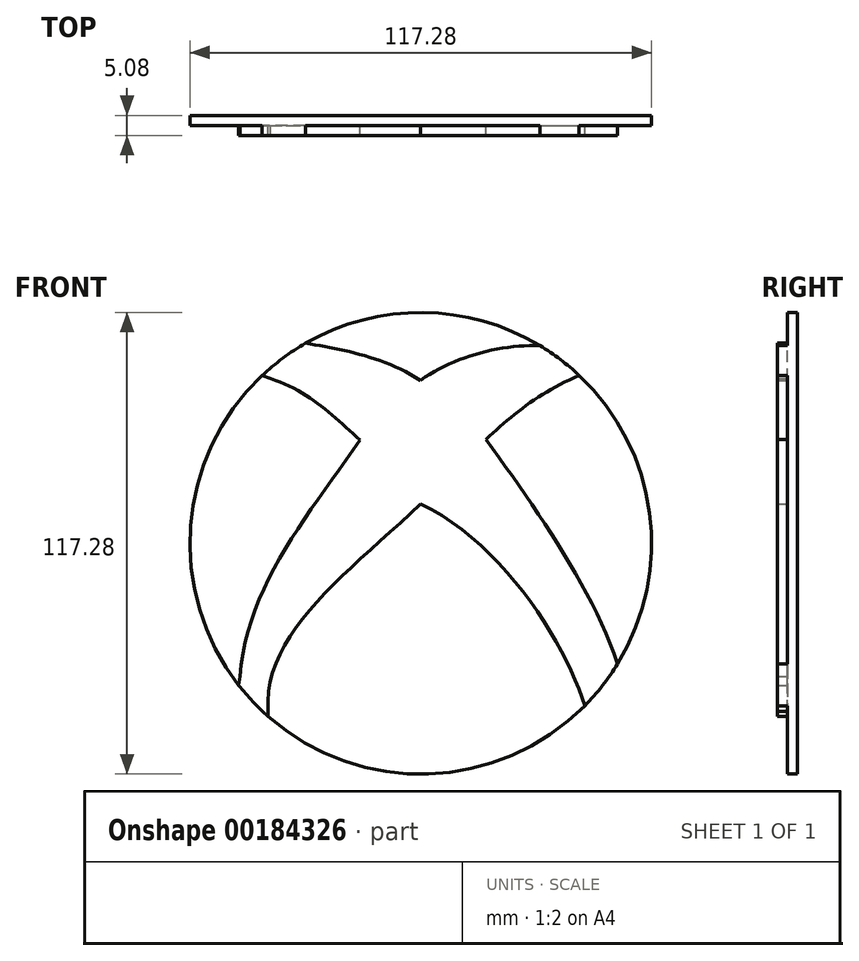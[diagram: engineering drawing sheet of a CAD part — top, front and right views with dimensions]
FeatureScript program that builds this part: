
annotation { "Feature Type Name" : "Feature", "Feature Type Description" : "" }
export const myFeature = defineFeature(function(context is Context, id is Id, definition is map)
    precondition{}
    {
        {
            var Q0;
            Q0=qCreatedBy(makeId("Front.planeOp"),FACE);
            var sketch = newSketch(context, id + "F0", { "sketchPlane" : qUnion([Q0])});
            skCircle(sketch, "E0", {"center": v(0, 0) * mm, "radius": 58.64 * mm});
            skPoint(sketch, "E1.1.internal.orphan", {"position": v(-4.16, 0) * mm});
            skPoint(sketch, "E1.2.internal.orphan", {"position": v(-4.36, 0) * mm});
            skFitSpline(sketch, "E2", {"points": [v(-38.19, 41.82) * mm, v(-15.47, 26.2) * mm], "startDerivative": vector(29.2, -9.13) * mm, "endDerivative": vector(20.69, -18.86) * mm});
            skFitSpline(sketch, "E3", {"points": [v(-15.47, 26.2) * mm, v(-45.9, -33.83) * mm], "startDerivative": vector(-40.16, -58.41) * mm, "endDerivative": vector(-4.87, -68.15) * mm});
            skFitSpline(sketch, "E4", {"points": [v(-38.8, -42.75) * mm, v(0, 9.98) * mm], "startDerivative": vector(-3.65, 59.63) * mm, "endDerivative": vector(59.8, 55.98) * mm});
            skFitSpline(sketch, "E5", {"points": [v(0, 9.98) * mm, v(41.66, -41.27) * mm], "startDerivative": vector(63.1, -29.94) * mm, "endDerivative": vector(14.55, -46.75) * mm});
            skFitSpline(sketch, "E6", {"points": [v(16.57, 26.4) * mm, v(50.03, -30.58) * mm], "startDerivative": vector(37.92, -52.45) * mm, "endDerivative": vector(20.08, -58.41) * mm});
            skFitSpline(sketch, "E7", {"points": [v(16.57, 26.4) * mm, v(40.25, 42.65) * mm], "startDerivative": vector(20.08, 18.86) * mm, "endDerivative": vector(29.05, 12.22) * mm});
            skFitSpline(sketch, "E8", {"points": [v(30.27, 50.22) * mm, v(0, 41.42) * mm], "startDerivative": vector(-30.14, 0.95) * mm, "endDerivative": vector(-25.37, -18.25) * mm});
            skFitSpline(sketch, "E9", {"points": [v(0, 41.42) * mm, v(-29.23, 50.84) * mm], "startDerivative": vector(-29.39, 18.25) * mm, "endDerivative": vector(-27.26, 4.54) * mm});
            skLineSegment(sketch, "E10", {"start": v(-45.9, -33.83) * mm, "end": v(-46.22, -36.09) * mm});
            skLineSegment(sketch, "E11", {"start": v(-38.8, -42.75) * mm, "end": v(-38.78, -43.98) * mm});
            skLineSegment(sketch, "E12", {"start": v(-38.19, 41.82) * mm, "end": v(-40.31, 42.59) * mm});
            skSolve(sketch);
        }
        {
            var Q0;
            Q0 = qSketchRegion(id + "F0", true);
            extrude(context, id + "F1", {"entities" : qUnion([Q0]), "depth" : 2.54 * mm});
        }
        {
            var Q0;
            Q0=makeQuery(id+"F0.imprint","IMPRINT",FACE,{"disambiguationData":[TD([[makeQuery(id+"F0.imprint","IMPRINT",EDGE,{"derivedFrom":sQuery(id+"F0.wireOp",EDGE,"E2")}),1.0]])]});
            extrude(context, id + "F2", {"entities" : qUnion([Q0]), "operationType" : NewBodyOperationType.ADD, "depth" : 5.08 * mm});
        }
    });
